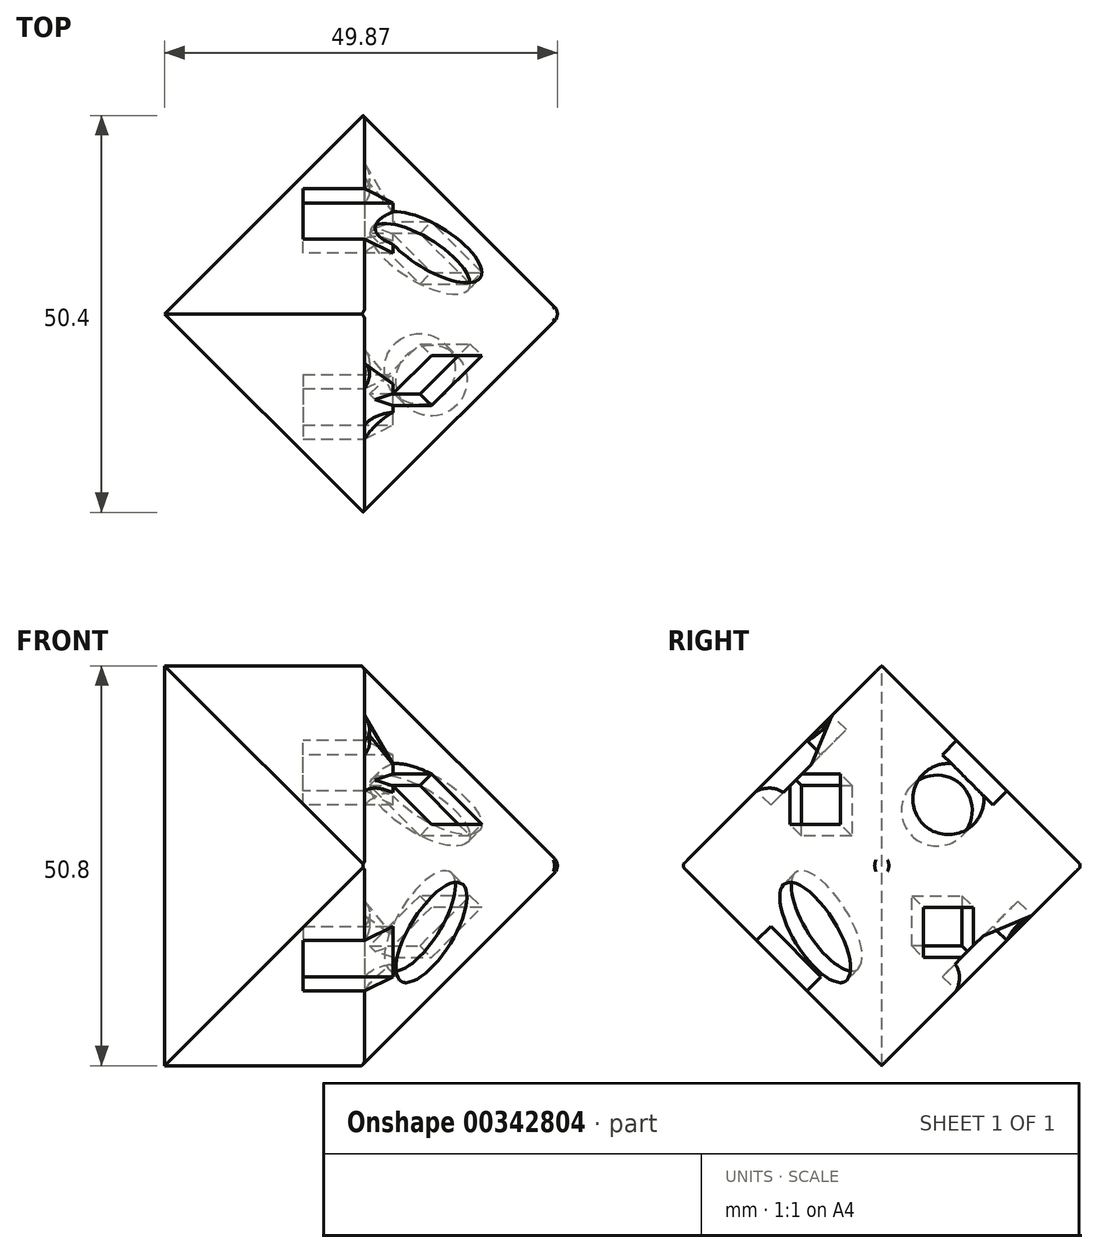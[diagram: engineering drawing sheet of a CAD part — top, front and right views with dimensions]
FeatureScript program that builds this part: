
annotation { "Feature Type Name" : "Feature", "Feature Type Description" : "" }
export const myFeature = defineFeature(function(context is Context, id is Id, definition is map)
    precondition{}
    {
        {
            var Q0;
            Q0=qCreatedBy(makeId("Top.planeOp"),FACE);
            var sketch = newSketch(context, id + "F0", { "sketchPlane" : qUnion([Q0])});
            skLineSegment(sketch, "E0.bottom", {"start": v(25.4, 25.4) * mm, "end": v(-25.4, 25.4) * mm});
            skLineSegment(sketch, "E0.top", {"start": v(25.4, -25.4) * mm, "end": v(-25.4, -25.4) * mm});
            skLineSegment(sketch, "E0.left", {"start": v(25.4, 25.4) * mm, "end": v(25.4, -25.4) * mm});
            skLineSegment(sketch, "E0.right", {"start": v(-25.4, 25.4) * mm, "end": v(-25.4, -25.4) * mm});
            skPoint(sketch, "E0.middle", {"position": v(0, 0) * mm});
            skSolve(sketch);
        }
        {
            var Q0;
            Q0 = qSketchRegion(id + "F0", true);
            extrude(context, id + "F1", {"entities" : qUnion([Q0]), "endBound" : BoundingType.SYMMETRIC, "depth" : 25.4 * mm});
        }
        {
            var Q0;
            Q0=makeQuery(id+"F1.opExtrude","SWEPT_FACE",FACE,{"disambiguationData":[OSD([sQuery(id+"F0.wireOp",EDGE,"E0.left")])]});
            var sketch = newSketch(context, id + "F2", { "sketchPlane" : qUnion([Q0])});
            skLineSegment(sketch, "E1.bottom", {"start": v(25.4, 25.4) * mm, "end": v(-25.4, 25.4) * mm});
            skLineSegment(sketch, "E1.top", {"start": v(25.4, -25.4) * mm, "end": v(-25.4, -25.4) * mm});
            skLineSegment(sketch, "E1.left", {"start": v(25.4, 25.4) * mm, "end": v(25.4, -25.4) * mm});
            skLineSegment(sketch, "E1.right", {"start": v(-25.4, 25.4) * mm, "end": v(-25.4, -25.4) * mm});
            skPoint(sketch, "E1.middle", {"position": v(0, 0) * mm});
            skSolve(sketch);
        }
        {
            var Q0;
            {var subQ0=sQuery(id+"F2.wireOp",EDGE,"E1.bottom");Q0=makeQuery(id+"F2.imprint","IMPRINT",FACE,{"disambiguationData":[TD([[makeQuery(id+"F2.imprint","IMPRINT",EDGE,{"derivedFrom":subQ0}),1.0]])]});}
            var Q1;
            {var subQ1=sQuery(id+"F0.wireOp",EDGE,"E0.left");var subQ2=makeQuery(id+"F1.opExtrude","CAP_EDGE",EDGE,{"disambiguationData":[OSD([subQ1])],"isStart":true});Q1=makeQuery(id+"F2.imprint","IMPRINT",FACE,{"disambiguationData":[TD([[makeQuery(id+"F2.imprint","IMPRINT",EDGE,{"derivedFrom":subQ2}),-1.0]])]});}
            var Q2;
            {var subQ0=sQuery(id+"F2.wireOp",EDGE,"E1.top");Q2=makeQuery(id+"F2.imprint","IMPRINT",FACE,{"disambiguationData":[TD([[makeQuery(id+"F2.imprint","IMPRINT",EDGE,{"derivedFrom":subQ0}),-1.0]])]});}
            var Q3;
            Q3=makeQuery(id+"F1.opExtrude","SWEPT_FACE",FACE,{"disambiguationData":[OSD([sQuery(id+"F0.wireOp",EDGE,"E0.right")])]});
            extrude(context, id + "F3", {"entities" : qUnion([Q0, Q1, Q2]), "operationType" : NewBodyOperationType.ADD, "endBound" : BoundingType.UP_TO_SURFACE, "oppositeDirection" : true, "endBoundEntityFace" : qUnion([Q3]), "depth" : 25.4 * mm});
        }
        {
            var Q0;
            Q0=makeQuery(id+"F3.opExtrude","TWEAK_EDGE",EDGE,{"derivedFrom":[makeQuery(id+"F1.opExtrude","SWEPT_FACE",FACE,{"disambiguationData":[OSD([sQuery(id+"F0.wireOp",EDGE,"E0.right")])]}),makeQuery(id+"F2.imprint","IMPRINT",EDGE,{"derivedFrom":sQuery(id+"F2.wireOp",EDGE,"E1.bottom")})]});
            var Q1;
            {var subQ0=sQuery(id+"F2.wireOp",EDGE,"E1.left");var subQ1=sQuery(id+"F0.wireOp",EDGE,"E0.left");var subQ2=makeQuery(id+"F2.imprint","INTERSECT",VERTEX,{"derivedFrom":[makeQuery(id+"F1.opExtrude","CAP_EDGE",EDGE,{"disambiguationData":[OSD([subQ1])],"isStart":true}),subQ0]});var subQ3=makeQuery(id+"F2.imprint","INTERSECT",VERTEX,{"derivedFrom":[makeQuery(id+"F1.opExtrude","CAP_EDGE",EDGE,{"disambiguationData":[OSD([subQ1])],"isStart":false}),subQ0]});var subQ4=sQuery(id+"F0.wireOp",EDGE,"E0.right");Q1=makeQuery(id+"F3.boolean.opBoolean","MERGE",EDGE,{"derivedFrom":[makeQuery(id+"F1.opExtrude","SWEPT_EDGE",EDGE,{"disambiguationData":[OSD([sQuery(id+"F0.wireOp",EDGE,"E0.bottom"),subQ4])]}),makeQuery(id+"F3.opExtrude","TWEAK_EDGE",EDGE,{"derivedFrom":[makeQuery(id+"F1.opExtrude","SWEPT_FACE",FACE,{"disambiguationData":[OSD([subQ4])]}),makeQuery(id+"F2.imprint","IMPRINT",EDGE,{"disambiguationData":[TD([[subQ3,1.0]])],"derivedFrom":subQ0}),makeQuery(id+"F2.imprint","IMPRINT",EDGE,{"disambiguationData":[TD([[subQ2,1.0]])],"derivedFrom":subQ0}),makeQuery(id+"F2.imprint","IMPRINT",EDGE,{"disambiguationData":[TD([[subQ2,-1.0]])],"derivedFrom":subQ0})]})]});}
            var Q2;
            Q2=makeQuery(id+"F3.opExtrude","SWEPT_EDGE",EDGE,{"disambiguationData":[OSD([sQuery(id+"F2.wireOp",EDGE,"E1.bottom"),sQuery(id+"F2.wireOp",EDGE,"E1.left")])]});
            var Q3;
            Q3=makeQuery(id+"F3.opExtrude","SWEPT_EDGE",EDGE,{"disambiguationData":[OSD([sQuery(id+"F2.wireOp",EDGE,"E1.top"),sQuery(id+"F2.wireOp",EDGE,"E1.left")])]});
            var Q4;
            Q4=makeQuery(id+"F3.opExtrude","TWEAK_EDGE",EDGE,{"derivedFrom":[makeQuery(id+"F1.opExtrude","SWEPT_FACE",FACE,{"disambiguationData":[OSD([sQuery(id+"F0.wireOp",EDGE,"E0.right")])]}),makeQuery(id+"F2.imprint","IMPRINT",EDGE,{"derivedFrom":sQuery(id+"F2.wireOp",EDGE,"E1.top")})]});
            var Q5;
            {var subQ0=sQuery(id+"F2.wireOp",EDGE,"E1.right");var subQ1=sQuery(id+"F0.wireOp",EDGE,"E0.left");var subQ2=makeQuery(id+"F2.imprint","INTERSECT",VERTEX,{"derivedFrom":[makeQuery(id+"F1.opExtrude","CAP_EDGE",EDGE,{"disambiguationData":[OSD([subQ1])],"isStart":true}),subQ0]});var subQ3=makeQuery(id+"F2.imprint","INTERSECT",VERTEX,{"derivedFrom":[makeQuery(id+"F1.opExtrude","CAP_EDGE",EDGE,{"disambiguationData":[OSD([subQ1])],"isStart":false}),subQ0]});var subQ4=sQuery(id+"F0.wireOp",EDGE,"E0.right");Q5=makeQuery(id+"F3.boolean.opBoolean","MERGE",EDGE,{"derivedFrom":[makeQuery(id+"F1.opExtrude","SWEPT_EDGE",EDGE,{"disambiguationData":[OSD([sQuery(id+"F0.wireOp",EDGE,"E0.top"),subQ4])]}),makeQuery(id+"F3.opExtrude","TWEAK_EDGE",EDGE,{"derivedFrom":[makeQuery(id+"F1.opExtrude","SWEPT_FACE",FACE,{"disambiguationData":[OSD([subQ4])]}),makeQuery(id+"F2.imprint","IMPRINT",EDGE,{"disambiguationData":[TD([[subQ3,1.0]])],"derivedFrom":subQ0}),makeQuery(id+"F2.imprint","IMPRINT",EDGE,{"disambiguationData":[TD([[subQ2,1.0]])],"derivedFrom":subQ0}),makeQuery(id+"F2.imprint","IMPRINT",EDGE,{"disambiguationData":[TD([[subQ2,-1.0]])],"derivedFrom":subQ0})]})]});}
            var Q6;
            Q6=makeQuery(id+"F3.opExtrude","SWEPT_EDGE",EDGE,{"disambiguationData":[OSD([sQuery(id+"F2.wireOp",EDGE,"E1.bottom"),sQuery(id+"F2.wireOp",EDGE,"E1.right")])]});
            var Q7;
            Q7=makeQuery(id+"F3.opExtrude","CAP_EDGE",EDGE,{"disambiguationData":[OSD([sQuery(id+"F2.wireOp",EDGE,"E1.bottom")])],"isStart":true});
            var Q8;
            Q8=makeQuery(id+"F3.boolean.opBoolean","MERGE",EDGE,{"derivedFrom":[makeQuery(id+"F1.opExtrude","SWEPT_EDGE",EDGE,{"disambiguationData":[OSD([sQuery(id+"F0.wireOp",EDGE,"E0.top"),sQuery(id+"F0.wireOp",EDGE,"E0.left")])]}),makeQuery(id+"F3.opExtrude","CAP_EDGE",EDGE,{"disambiguationData":[OSD([sQuery(id+"F2.wireOp",EDGE,"E1.right")])],"isStart":true})]});
            var Q9;
            Q9=makeQuery(id+"F3.boolean.opBoolean","MERGE",EDGE,{"derivedFrom":[makeQuery(id+"F1.opExtrude","SWEPT_EDGE",EDGE,{"disambiguationData":[OSD([sQuery(id+"F0.wireOp",EDGE,"E0.bottom"),sQuery(id+"F0.wireOp",EDGE,"E0.left")])]}),makeQuery(id+"F3.opExtrude","CAP_EDGE",EDGE,{"disambiguationData":[OSD([sQuery(id+"F2.wireOp",EDGE,"E1.left")])],"isStart":true})]});
            var Q10;
            Q10=makeQuery(id+"F3.opExtrude","CAP_EDGE",EDGE,{"disambiguationData":[OSD([sQuery(id+"F2.wireOp",EDGE,"E1.top")])],"isStart":true});
            var Q11;
            Q11=makeQuery(id+"F3.opExtrude","SWEPT_EDGE",EDGE,{"disambiguationData":[OSD([sQuery(id+"F2.wireOp",EDGE,"E1.top"),sQuery(id+"F2.wireOp",EDGE,"E1.right")])]});
            chamfer(context, id + "F4", {"entities" : qUnion([Q0, Q1, Q2, Q3, Q4, Q5, Q6, Q7, Q8, Q9, Q10, Q11]), "width" : 25.4 * mm, "tangentPropagation" : true});
        }
        {
            var Q0;
            Q0=makeQuery(id+"F4.opChamfer","BLEND_FACE",FACE,{"disambiguationData":[OSD([sQuery(id+"F0.wireOp",EDGE,"E0.right"),sQuery(id+"F2.wireOp",EDGE,"E1.bottom"),sQuery(id+"F2.wireOp",EDGE,"E1.left")])]});
            var sketch = newSketch(context, id + "F5", { "sketchPlane" : qUnion([Q0])});
            skCircle(sketch, "E2", {"center": v(0, 0) * mm, "radius": 7.83 * mm});
            skLineSegment(sketch, "E3", {"start": v(5.18, -8.98) * mm, "end": v(3.91, -6.78) * mm});
            skLineSegment(sketch, "E4.bottom", {"start": v(7.83, -4.52) * mm, "end": v(-7.83, -4.52) * mm});
            skLineSegment(sketch, "E4.top", {"start": v(7.83, 4.52) * mm, "end": v(-7.83, 4.52) * mm});
            skLineSegment(sketch, "E4.left", {"start": v(7.83, -4.52) * mm, "end": v(7.83, 4.52) * mm});
            skLineSegment(sketch, "E4.right", {"start": v(-7.83, -4.52) * mm, "end": v(-7.83, 4.52) * mm});
            skEllipse(sketch, "E5", {"center": v(0, 0) * mm, "majorRadius": 7.83 * mm, "minorRadius": 4.52 * mm, "majorAxis": v(-1, 0)});
            skSolve(sketch);
        }
        {
            var Q0;
            {var subQ0=sQuery(id+"F5.wireOp",EDGE,"E5");var subQ1=makeQuery(id+"F5.imprint","INTERSECT",VERTEX,{"derivedFrom":[sQuery(id+"F5.wireOp",EDGE,"E4.bottom"),subQ0]});Q0=makeQuery(id+"F5.imprint","IMPRINT",FACE,{"disambiguationData":[TD([[makeQuery(id+"F5.imprint","IMPRINT",EDGE,{"disambiguationData":[TD([[subQ1,1.0]])],"derivedFrom":subQ0}),1.0]])]});}
            extrude(context, id + "F6", {"entities" : qUnion([Q0]), "operationType" : NewBodyOperationType.REMOVE, "oppositeDirection" : true, "depth" : 2.54 * mm});
        }
        {
            var Q0;
            Q0=makeQuery(id+"F4.opChamfer","BLEND_FACE",FACE,{"disambiguationData":[OSD([sQuery(id+"F0.wireOp",EDGE,"E0.right"),sQuery(id+"F2.wireOp",EDGE,"E1.bottom"),sQuery(id+"F2.wireOp",EDGE,"E1.right")])]});
            var sketch = newSketch(context, id + "F7", { "sketchPlane" : qUnion([Q0])});
            skLineSegment(sketch, "E6.bottom", {"start": v(7.83, -4.52) * mm, "end": v(-7.83, -4.52) * mm});
            skLineSegment(sketch, "E6.top", {"start": v(7.83, 4.52) * mm, "end": v(-7.83, 4.52) * mm});
            skLineSegment(sketch, "E6.left", {"start": v(7.83, -4.52) * mm, "end": v(7.83, 4.52) * mm});
            skLineSegment(sketch, "E6.right", {"start": v(-7.83, -4.52) * mm, "end": v(-7.83, 4.52) * mm});
            skPoint(sketch, "E6.middle", {"position": v(0, 0) * mm});
            skLineSegment(sketch, "E7", {"start": v(0, 4.52) * mm, "end": v(7.83, 0) * mm});
            skLineSegment(sketch, "E8", {"start": v(7.83, 0) * mm, "end": v(0, -4.52) * mm});
            skLineSegment(sketch, "E9", {"start": v(0, -4.52) * mm, "end": v(-7.83, 0) * mm});
            skLineSegment(sketch, "E10", {"start": v(-7.83, 0) * mm, "end": v(0, 4.52) * mm});
            skSolve(sketch);
        }
        {
            var Q0;
            Q0=makeQuery(id+"F7.imprint","IMPRINT",FACE,{"disambiguationData":[TD([[makeQuery(id+"F7.imprint","IMPRINT",EDGE,{"derivedFrom":sQuery(id+"F7.wireOp",EDGE,"E7")}),-1.0]])]});
            extrude(context, id + "F8", {"entities" : qUnion([Q0]), "operationType" : NewBodyOperationType.REMOVE, "oppositeDirection" : true, "depth" : 2.54 * mm});
        }
        {
            var Q0;
            Q0=makeQuery(id+"F4.opChamfer","BLEND_FACE",FACE,{"disambiguationData":[OSD([sQuery(id+"F2.wireOp",EDGE,"E1.top"),sQuery(id+"F2.wireOp",EDGE,"E1.left")])]});
            var sketch = newSketch(context, id + "F9", { "sketchPlane" : qUnion([Q0])});
            skLineSegment(sketch, "E11.bottom", {"start": v(7.83, -4.52) * mm, "end": v(-7.83, -4.52) * mm});
            skLineSegment(sketch, "E11.top", {"start": v(7.83, 4.52) * mm, "end": v(-7.83, 4.52) * mm});
            skLineSegment(sketch, "E11.left", {"start": v(7.83, -4.52) * mm, "end": v(7.83, 4.52) * mm});
            skLineSegment(sketch, "E11.right", {"start": v(-7.83, -4.52) * mm, "end": v(-7.83, 4.52) * mm});
            skPoint(sketch, "E11.middle", {"position": v(0, 0) * mm});
            skLineSegment(sketch, "E12", {"start": v(0, 4.52) * mm, "end": v(7.83, 0) * mm});
            skLineSegment(sketch, "E13", {"start": v(7.83, 0) * mm, "end": v(0, -4.52) * mm});
            skLineSegment(sketch, "E14", {"start": v(0, -4.52) * mm, "end": v(-7.83, 0) * mm});
            skLineSegment(sketch, "E15", {"start": v(-7.83, 0) * mm, "end": v(0, 4.52) * mm});
            skSolve(sketch);
        }
        {
            var Q0;
            Q0=makeQuery(id+"F9.imprint","IMPRINT",FACE,{"disambiguationData":[TD([[makeQuery(id+"F9.imprint","IMPRINT",EDGE,{"derivedFrom":sQuery(id+"F9.wireOp",EDGE,"E12")}),-1.0]])]});
            extrude(context, id + "F10", {"entities" : qUnion([Q0]), "operationType" : NewBodyOperationType.REMOVE, "oppositeDirection" : true, "depth" : 2.54 * mm});
        }
        {
            var Q0;
            Q0=makeQuery(id+"F4.opChamfer","BLEND_FACE",FACE,{"disambiguationData":[OSD([sQuery(id+"F2.wireOp",EDGE,"E1.top"),sQuery(id+"F2.wireOp",EDGE,"E1.right")])]});
            var sketch = newSketch(context, id + "F11", { "sketchPlane" : qUnion([Q0])});
            skLineSegment(sketch, "E16.bottom", {"start": v(7.83, 4.52) * mm, "end": v(0, -9.04) * mm});
            skLineSegment(sketch, "E16.top", {"start": v(0, 9.04) * mm, "end": v(-7.83, -4.52) * mm});
            skLineSegment(sketch, "E16.left", {"start": v(7.83, 4.52) * mm, "end": v(0, 9.04) * mm});
            skLineSegment(sketch, "E16.right", {"start": v(0, -9.04) * mm, "end": v(-7.83, -4.52) * mm});
            skPoint(sketch, "E16.middle", {"position": v(0, 0) * mm});
            skEllipse(sketch, "E17", {"center": v(0, 0) * mm, "majorRadius": 7.83 * mm, "minorRadius": 4.52 * mm, "majorAxis": v(-0.5, -0.87)});
            skSolve(sketch);
        }
        {
            var Q0;
            {var subQ0=sQuery(id+"F11.wireOp",EDGE,"E17");var subQ1=makeQuery(id+"F11.imprint","INTERSECT",VERTEX,{"derivedFrom":[sQuery(id+"F11.wireOp",EDGE,"E16.bottom"),subQ0]});Q0=makeQuery(id+"F11.imprint","IMPRINT",FACE,{"disambiguationData":[TD([[makeQuery(id+"F11.imprint","IMPRINT",EDGE,{"disambiguationData":[TD([[subQ1,1.0]])],"derivedFrom":subQ0}),1.0]])]});}
            extrude(context, id + "F12", {"entities" : qUnion([Q0]), "operationType" : NewBodyOperationType.REMOVE, "oppositeDirection" : true, "depth" : 2.54 * mm});
        }
        {
            var Q0;
            Q0=makeQuery(id+"F4.opChamfer","BLEND_FACE",FACE,{"disambiguationData":[OSD([sQuery(id+"F2.wireOp",EDGE,"E1.bottom"),sQuery(id+"F2.wireOp",EDGE,"E1.left")])]});
            var sketch = newSketch(context, id + "F13", { "sketchPlane" : qUnion([Q0])});
            skLineSegment(sketch, "E18.bottom", {"start": v(-7.83, -4.52) * mm, "end": v(7.83, -4.52) * mm});
            skLineSegment(sketch, "E18.top", {"start": v(-7.83, 4.52) * mm, "end": v(7.83, 4.52) * mm});
            skLineSegment(sketch, "E18.left", {"start": v(-7.83, -4.52) * mm, "end": v(-7.83, 4.52) * mm});
            skLineSegment(sketch, "E18.right", {"start": v(7.83, -4.52) * mm, "end": v(7.83, 4.52) * mm});
            skPoint(sketch, "E18.middle", {"position": v(0, 0) * mm});
            skSolve(sketch);
        }
        {
            var Q0;
            Q0=makeQuery(id+"F13.imprint","IMPRINT",FACE,{"disambiguationData":[TD([[makeQuery(id+"F13.imprint","IMPRINT",EDGE,{"derivedFrom":sQuery(id+"F13.wireOp",EDGE,"E18.bottom")}),1.0]])]});
            extrude(context, id + "F14", {"entities" : qUnion([Q0]), "operationType" : NewBodyOperationType.REMOVE, "oppositeDirection" : true, "depth" : 2.54 * mm});
        }
        {
            var Q0;
            Q0=makeQuery(id+"F4.opChamfer","BLEND_FACE",FACE,{"disambiguationData":[OSD([sQuery(id+"F0.wireOp",EDGE,"E0.right"),sQuery(id+"F2.wireOp",EDGE,"E1.top"),sQuery(id+"F2.wireOp",EDGE,"E1.right")])]});
            var sketch = newSketch(context, id + "F15", { "sketchPlane" : qUnion([Q0])});
            skLineSegment(sketch, "E19.bottom", {"start": v(-7.83, -4.52) * mm, "end": v(7.83, -4.52) * mm});
            skLineSegment(sketch, "E19.top", {"start": v(-7.83, 4.52) * mm, "end": v(7.83, 4.52) * mm});
            skLineSegment(sketch, "E19.left", {"start": v(-7.83, -4.52) * mm, "end": v(-7.83, 4.52) * mm});
            skLineSegment(sketch, "E19.right", {"start": v(7.83, -4.52) * mm, "end": v(7.83, 4.52) * mm});
            skPoint(sketch, "E19.middle", {"position": v(0, 0) * mm});
            skSolve(sketch);
        }
        {
            var Q0;
            Q0=makeQuery(id+"F15.imprint","IMPRINT",FACE,{"disambiguationData":[TD([[makeQuery(id+"F15.imprint","IMPRINT",EDGE,{"derivedFrom":sQuery(id+"F15.wireOp",EDGE,"E19.bottom")}),1.0]])]});
            extrude(context, id + "F16", {"entities" : qUnion([Q0]), "operationType" : NewBodyOperationType.REMOVE, "oppositeDirection" : true, "depth" : 2.54 * mm});
        }
        {
            var Q0;
            Q0=makeQuery(id+"F4.opChamfer","BLEND_FACE",FACE,{"disambiguationData":[OSD([sQuery(id+"F2.wireOp",EDGE,"E1.bottom"),sQuery(id+"F2.wireOp",EDGE,"E1.right")])]});
            var sketch = newSketch(context, id + "F17", { "sketchPlane" : qUnion([Q0])});
            skLineSegment(sketch, "E20.bottom", {"start": v(7.83, -4.52) * mm, "end": v(0, 9.04) * mm});
            skLineSegment(sketch, "E20.top", {"start": v(0, -9.04) * mm, "end": v(-7.83, 4.52) * mm});
            skLineSegment(sketch, "E20.left", {"start": v(7.83, -4.52) * mm, "end": v(0, -9.04) * mm});
            skLineSegment(sketch, "E20.right", {"start": v(0, 9.04) * mm, "end": v(-7.83, 4.52) * mm});
            skPoint(sketch, "E20.middle", {"position": v(0, 0) * mm});
            skCircle(sketch, "E21", {"center": v(3.91, -6.78) * mm, "radius": 4.52 * mm});
            skCircle(sketch, "E22", {"center": v(-3.91, 6.78) * mm, "radius": 4.52 * mm});
            skSolve(sketch);
        }
        {
            var Q0;
            {var subQ0=sQuery(id+"F17.wireOp",EDGE,"E20.bottom");Q0=makeQuery(id+"F17.imprint","IMPRINT",FACE,{"disambiguationData":[TD([[makeQuery(id+"F17.imprint","IMPRINT",EDGE,{"derivedFrom":subQ0}),1.0]])]});}
            extrude(context, id + "F18", {"entities" : qUnion([Q0]), "operationType" : NewBodyOperationType.REMOVE, "oppositeDirection" : true, "depth" : 2.54 * mm});
        }
        {
            var Q0;
            Q0=makeQuery(id+"F4.opChamfer","BLEND_FACE",FACE,{"disambiguationData":[OSD([sQuery(id+"F0.wireOp",EDGE,"E0.right"),sQuery(id+"F2.wireOp",EDGE,"E1.top"),sQuery(id+"F2.wireOp",EDGE,"E1.left")])]});
            var sketch = newSketch(context, id + "F19", { "sketchPlane" : qUnion([Q0])});
            skLineSegment(sketch, "E23.bottom", {"start": v(0, 9.04) * mm, "end": v(-7.83, -4.52) * mm});
            skLineSegment(sketch, "E23.top", {"start": v(7.83, 4.52) * mm, "end": v(0, -9.04) * mm});
            skLineSegment(sketch, "E23.left", {"start": v(0, 9.04) * mm, "end": v(7.83, 4.52) * mm});
            skLineSegment(sketch, "E23.right", {"start": v(-7.83, -4.52) * mm, "end": v(0, -9.04) * mm});
            skPoint(sketch, "E23.middle", {"position": v(0, 0) * mm});
            skCircle(sketch, "E24", {"center": v(3.91, 6.78) * mm, "radius": 4.52 * mm});
            skCircle(sketch, "E25", {"center": v(-3.91, -6.78) * mm, "radius": 4.52 * mm});
            skSolve(sketch);
        }
        {
            var Q0;
            {var subQ0=sQuery(id+"F19.wireOp",EDGE,"E23.bottom");Q0=makeQuery(id+"F19.imprint","IMPRINT",FACE,{"disambiguationData":[TD([[makeQuery(id+"F19.imprint","IMPRINT",EDGE,{"derivedFrom":subQ0}),1.0]])]});}
            extrude(context, id + "F20", {"entities" : qUnion([Q0]), "operationType" : NewBodyOperationType.REMOVE, "oppositeDirection" : true, "depth" : 2.54 * mm});
        }
        {
            var Q0;
            {var subQ0=sQuery(id+"F2.wireOp",EDGE,"E1.right");var subQ1=sQuery(id+"F2.wireOp",EDGE,"E1.bottom");Q0=makeQuery(id+"F4.opChamfer","BLEND_EDGE",EDGE,{"blendedFrom":[makeQuery(id+"F3.opExtrude","CAP_VERTEX",VERTEX,{"disambiguationData":[OSD([sQuery(id+"F0.wireOp",EDGE,"E0.right"),subQ1,subQ0])],"isStart":false}),makeQuery(id+"F3.opExtrude","CAP_VERTEX",VERTEX,{"disambiguationData":[OSD([subQ1,subQ0])],"isStart":true})],"blendedInto":[]});}
            var Q1;
            {var subQ0=sQuery(id+"F2.wireOp",EDGE,"E1.bottom");Q1=makeQuery(id+"F4.opChamfer","BLEND_EDGE",EDGE,{"blendedFrom":[makeQuery(id+"F3.opExtrude","CAP_VERTEX",VERTEX,{"disambiguationData":[OSD([subQ0,sQuery(id+"F2.wireOp",EDGE,"E1.left")])],"isStart":true}),makeQuery(id+"F3.opExtrude","CAP_VERTEX",VERTEX,{"disambiguationData":[OSD([subQ0,sQuery(id+"F2.wireOp",EDGE,"E1.right")])],"isStart":true})],"blendedInto":[]});}
            var Q2;
            {var subQ0=sQuery(id+"F2.wireOp",EDGE,"E1.right");Q2=makeQuery(id+"F4.opChamfer","BLEND_EDGE",EDGE,{"blendedFrom":[makeQuery(id+"F3.opExtrude","CAP_VERTEX",VERTEX,{"disambiguationData":[OSD([sQuery(id+"F2.wireOp",EDGE,"E1.bottom"),subQ0])],"isStart":true}),makeQuery(id+"F3.opExtrude","CAP_VERTEX",VERTEX,{"disambiguationData":[OSD([sQuery(id+"F2.wireOp",EDGE,"E1.top"),subQ0])],"isStart":true})],"blendedInto":[]});}
            var Q3;
            {var subQ0=sQuery(id+"F2.wireOp",EDGE,"E1.bottom");var subQ1=sQuery(id+"F0.wireOp",EDGE,"E0.right");Q3=makeQuery(id+"F4.opChamfer","BLEND_EDGE",EDGE,{"blendedFrom":[makeQuery(id+"F3.opExtrude","CAP_VERTEX",VERTEX,{"disambiguationData":[OSD([subQ1,subQ0,sQuery(id+"F2.wireOp",EDGE,"E1.left")])],"isStart":false}),makeQuery(id+"F3.opExtrude","CAP_VERTEX",VERTEX,{"disambiguationData":[OSD([subQ1,subQ0,sQuery(id+"F2.wireOp",EDGE,"E1.right")])],"isStart":false})],"blendedInto":[]});}
            var Q4;
            {var subQ0=sQuery(id+"F2.wireOp",EDGE,"E1.left");var subQ1=sQuery(id+"F2.wireOp",EDGE,"E1.bottom");Q4=makeQuery(id+"F4.opChamfer","BLEND_EDGE",EDGE,{"blendedFrom":[makeQuery(id+"F3.opExtrude","CAP_VERTEX",VERTEX,{"disambiguationData":[OSD([sQuery(id+"F0.wireOp",EDGE,"E0.right"),subQ1,subQ0])],"isStart":false}),makeQuery(id+"F3.opExtrude","CAP_VERTEX",VERTEX,{"disambiguationData":[OSD([subQ1,subQ0])],"isStart":true})],"blendedInto":[]});}
            var Q5;
            {var subQ0=sQuery(id+"F2.wireOp",EDGE,"E1.right");var subQ1=sQuery(id+"F0.wireOp",EDGE,"E0.right");Q5=makeQuery(id+"F4.opChamfer","BLEND_EDGE",EDGE,{"blendedFrom":[makeQuery(id+"F3.opExtrude","CAP_VERTEX",VERTEX,{"disambiguationData":[OSD([subQ1,sQuery(id+"F2.wireOp",EDGE,"E1.bottom"),subQ0])],"isStart":false}),makeQuery(id+"F3.opExtrude","CAP_VERTEX",VERTEX,{"disambiguationData":[OSD([subQ1,sQuery(id+"F2.wireOp",EDGE,"E1.top"),subQ0])],"isStart":false})],"blendedInto":[]});}
            var Q6;
            {var subQ0=sQuery(id+"F2.wireOp",EDGE,"E1.left");var subQ1=sQuery(id+"F0.wireOp",EDGE,"E0.right");Q6=makeQuery(id+"F4.opChamfer","BLEND_EDGE",EDGE,{"blendedFrom":[makeQuery(id+"F3.opExtrude","CAP_VERTEX",VERTEX,{"disambiguationData":[OSD([subQ1,sQuery(id+"F2.wireOp",EDGE,"E1.bottom"),subQ0])],"isStart":false}),makeQuery(id+"F3.opExtrude","CAP_VERTEX",VERTEX,{"disambiguationData":[OSD([subQ1,sQuery(id+"F2.wireOp",EDGE,"E1.top"),subQ0])],"isStart":false})],"blendedInto":[]});}
            var Q7;
            {var subQ0=sQuery(id+"F2.wireOp",EDGE,"E1.left");var subQ1=sQuery(id+"F2.wireOp",EDGE,"E1.top");Q7=makeQuery(id+"F4.opChamfer","BLEND_EDGE",EDGE,{"blendedFrom":[makeQuery(id+"F3.opExtrude","CAP_VERTEX",VERTEX,{"disambiguationData":[OSD([sQuery(id+"F0.wireOp",EDGE,"E0.right"),subQ1,subQ0])],"isStart":false}),makeQuery(id+"F3.opExtrude","CAP_VERTEX",VERTEX,{"disambiguationData":[OSD([subQ1,subQ0])],"isStart":true})],"blendedInto":[]});}
            var Q8;
            {var subQ0=sQuery(id+"F2.wireOp",EDGE,"E1.top");Q8=makeQuery(id+"F4.opChamfer","BLEND_EDGE",EDGE,{"blendedFrom":[makeQuery(id+"F3.opExtrude","CAP_VERTEX",VERTEX,{"disambiguationData":[OSD([subQ0,sQuery(id+"F2.wireOp",EDGE,"E1.left")])],"isStart":true}),makeQuery(id+"F3.opExtrude","CAP_VERTEX",VERTEX,{"disambiguationData":[OSD([subQ0,sQuery(id+"F2.wireOp",EDGE,"E1.right")])],"isStart":true})],"blendedInto":[]});}
            var Q9;
            {var subQ0=sQuery(id+"F2.wireOp",EDGE,"E1.left");Q9=makeQuery(id+"F4.opChamfer","BLEND_EDGE",EDGE,{"blendedFrom":[makeQuery(id+"F3.opExtrude","CAP_VERTEX",VERTEX,{"disambiguationData":[OSD([sQuery(id+"F2.wireOp",EDGE,"E1.bottom"),subQ0])],"isStart":true}),makeQuery(id+"F3.opExtrude","CAP_VERTEX",VERTEX,{"disambiguationData":[OSD([sQuery(id+"F2.wireOp",EDGE,"E1.top"),subQ0])],"isStart":true})],"blendedInto":[]});}
            var Q10;
            {var subQ0=sQuery(id+"F2.wireOp",EDGE,"E1.right");var subQ1=sQuery(id+"F2.wireOp",EDGE,"E1.top");Q10=makeQuery(id+"F4.opChamfer","BLEND_EDGE",EDGE,{"blendedFrom":[makeQuery(id+"F3.opExtrude","CAP_VERTEX",VERTEX,{"disambiguationData":[OSD([sQuery(id+"F0.wireOp",EDGE,"E0.right"),subQ1,subQ0])],"isStart":false}),makeQuery(id+"F3.opExtrude","CAP_VERTEX",VERTEX,{"disambiguationData":[OSD([subQ1,subQ0])],"isStart":true})],"blendedInto":[]});}
            var Q11;
            {var subQ0=sQuery(id+"F2.wireOp",EDGE,"E1.top");var subQ1=sQuery(id+"F0.wireOp",EDGE,"E0.right");Q11=makeQuery(id+"F4.opChamfer","BLEND_EDGE",EDGE,{"blendedFrom":[makeQuery(id+"F3.opExtrude","CAP_VERTEX",VERTEX,{"disambiguationData":[OSD([subQ1,subQ0,sQuery(id+"F2.wireOp",EDGE,"E1.left")])],"isStart":false}),makeQuery(id+"F3.opExtrude","CAP_VERTEX",VERTEX,{"disambiguationData":[OSD([subQ1,subQ0,sQuery(id+"F2.wireOp",EDGE,"E1.right")])],"isStart":false})],"blendedInto":[]});}
            fillet(context, id + "F21", {"entities" : qUnion([Q0, Q1, Q2, Q3, Q4, Q5, Q6, Q7, Q8, Q9, Q10, Q11]), "radius" : 1.27 * mm, "tangentPropagation" : true, "allowEdgeOverflow" : false});
        }
    });
